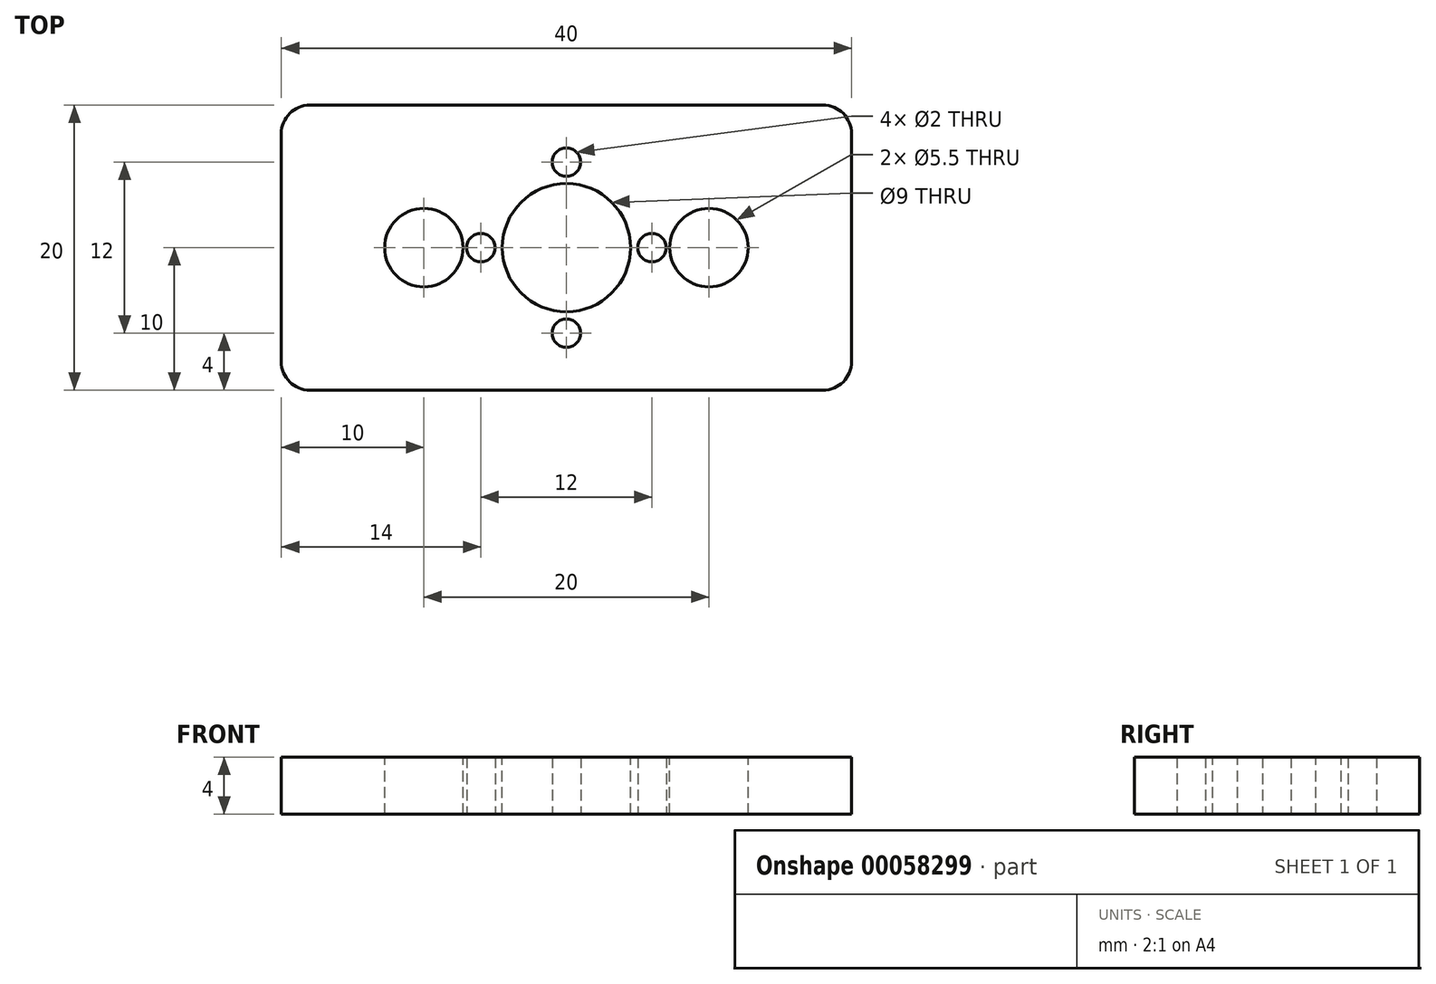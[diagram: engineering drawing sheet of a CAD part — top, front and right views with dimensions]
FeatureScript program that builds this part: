
annotation { "Feature Type Name" : "Feature", "Feature Type Description" : "" }
export const myFeature = defineFeature(function(context is Context, id is Id, definition is map)
    precondition{}
    {
        {
            var Q0;
            Q0=qCreatedBy(makeId("Top.planeOp"),FACE);
            var sketch = newSketch(context, id + "F6", { "sketchPlane" : qUnion([Q0])});
            skLineSegment(sketch, "E0.rect.bottom", {"start": v(20, -10) * mm, "end": v(-20, -10) * mm});
            skLineSegment(sketch, "E0.rect.top", {"start": v(20, 10) * mm, "end": v(-20, 10) * mm});
            skLineSegment(sketch, "E0.rect.left", {"start": v(20, -10) * mm, "end": v(20, 10) * mm});
            skLineSegment(sketch, "E0.rect.right", {"start": v(-20, -10) * mm, "end": v(-20, 10) * mm});
            skPoint(sketch, "E0.rect.middle", {"position": v(0, 0) * mm});
            skCircle(sketch, "E1", {"center": v(0, 0) * mm, "radius": 6 * mm});
            skPoint(sketch, "E2", {"position": v(0, 6) * mm});
            skPoint(sketch, "E3", {"position": v(6, 0) * mm});
            skPoint(sketch, "E4", {"position": v(0, -6) * mm});
            skPoint(sketch, "E5", {"position": v(-6, 0) * mm});
            skSolve(sketch);
        }
        {
            var Q0;
            Q0=makeQuery(id+"F6.imprint","IMPRINT",FACE,{"disambiguationData":[TD([[makeQuery(id+"F6.imprint","IMPRINT",EDGE,{"derivedFrom":sQuery(id+"F6.wireOp",EDGE,"E0.rect.bottom")}),-1.0]])]});
            var Q1;
            Q1=makeQuery(id+"F6.imprint","IMPRINT",FACE,{"disambiguationData":[TD([[makeQuery(id+"F6.imprint","IMPRINT",EDGE,{"derivedFrom":sQuery(id+"F6.wireOp",EDGE,"E1")}),1.0]])]});
            extrude(context, id + "F7", {"entities" : qUnion([Q0, Q1]), "depth" : 4 * mm});
        }
        {
            var Q0;
            Q0=sQuery(id+"F6.wireOp",VERTEX,"E4");
            var Q1;
            Q1=sQuery(id+"F6.wireOp",VERTEX,"E5");
            var Q2;
            Q2=sQuery(id+"F6.wireOp",VERTEX,"E3");
            var Q3;
            Q3=sQuery(id+"F6.wireOp",VERTEX,"E2");
            var Q4;
            Q4=makeQuery(id+"F7.opExtrude","SWEPT_BODY",BODY,{"disambiguationData":[OSD([sQuery(id+"F6.wireOp",EDGE,"E0.rect.bottom"),sQuery(id+"F6.wireOp",EDGE,"E0.rect.top"),sQuery(id+"F6.wireOp",EDGE,"E0.rect.left"),sQuery(id+"F6.wireOp",EDGE,"E0.rect.right")])]});
            hole(context, id + "F0", {"style" : HoleStyle.SIMPLE, "holeDiameter" : 2 * mm, "endStyle" : HoleEndStyle.THROUGH, "oppositeDirection" : true, "locations" : qUnion([Q0, Q1, Q2, Q3]), "scope" : qUnion([Q4])});
        }
        {
            var Q0;
            Q0=makeQuery(id+"F7.opExtrude","CAP_FACE",FACE,{"disambiguationData":[OSD([sQuery(id+"F6.wireOp",EDGE,"E0.rect.bottom"),sQuery(id+"F6.wireOp",EDGE,"E0.rect.top"),sQuery(id+"F6.wireOp",EDGE,"E0.rect.left"),sQuery(id+"F6.wireOp",EDGE,"E0.rect.right")])],"isStart":false});
            var sketch = newSketch(context, id + "F8", { "sketchPlane" : qUnion([Q0])});
            skPoint(sketch, "E6", {"position": v(0, 0) * mm});
            skSolve(sketch);
        }
        {
            var Q0;
            Q0=sQuery(id+"F8.wireOp",VERTEX,"E6");
            var Q1;
            Q1=makeQuery(id+"F7.opExtrude","SWEPT_BODY",BODY,{"disambiguationData":[OSD([sQuery(id+"F6.wireOp",EDGE,"E0.rect.bottom"),sQuery(id+"F6.wireOp",EDGE,"E0.rect.top"),sQuery(id+"F6.wireOp",EDGE,"E0.rect.left"),sQuery(id+"F6.wireOp",EDGE,"E0.rect.right")])]});
            hole(context, id + "F1", {"style" : HoleStyle.SIMPLE, "holeDiameter" : 9 * mm, "endStyle" : HoleEndStyle.THROUGH, "locations" : qUnion([Q0]), "scope" : qUnion([Q1])});
        }
        {
            var Q0;
            Q0=makeQuery(id+"F7.opExtrude","SWEPT_EDGE",EDGE,{"disambiguationData":[OSD([sQuery(id+"F6.wireOp",EDGE,"E0.rect.top"),sQuery(id+"F6.wireOp",EDGE,"E0.rect.left")])]});
            var Q1;
            Q1=makeQuery(id+"F7.opExtrude","SWEPT_EDGE",EDGE,{"disambiguationData":[OSD([sQuery(id+"F6.wireOp",EDGE,"E0.rect.bottom"),sQuery(id+"F6.wireOp",EDGE,"E0.rect.left")])]});
            var Q2;
            Q2=makeQuery(id+"F7.opExtrude","SWEPT_EDGE",EDGE,{"disambiguationData":[OSD([sQuery(id+"F6.wireOp",EDGE,"E0.rect.bottom"),sQuery(id+"F6.wireOp",EDGE,"E0.rect.right")])]});
            var Q3;
            Q3=makeQuery(id+"F7.opExtrude","SWEPT_EDGE",EDGE,{"disambiguationData":[OSD([sQuery(id+"F6.wireOp",EDGE,"E0.rect.top"),sQuery(id+"F6.wireOp",EDGE,"E0.rect.right")])]});
            fillet(context, id + "F2", {"entities" : qUnion([Q0, Q1, Q2, Q3]), "radius" : 2 * mm, "tangentPropagation" : true, "allowEdgeOverflow" : false});
        }
        {
            var Q0;
            Q0=makeQuery(id+"F7.opExtrude","CAP_FACE",FACE,{"disambiguationData":[OSD([sQuery(id+"F6.wireOp",EDGE,"E0.rect.bottom"),sQuery(id+"F6.wireOp",EDGE,"E0.rect.top"),sQuery(id+"F6.wireOp",EDGE,"E0.rect.left"),sQuery(id+"F6.wireOp",EDGE,"E0.rect.right")])],"isStart":false});
            var sketch = newSketch(context, id + "F3", { "sketchPlane" : qUnion([Q0])});
            skPoint(sketch, "E7", {"position": v(-10, 0) * mm});
            skPoint(sketch, "E8", {"position": v(10, 0) * mm});
            skSolve(sketch);
        }
        {
            var Q0;
            Q0=sQuery(id+"F3.wireOp",VERTEX,"E8");
            var Q1;
            Q1=sQuery(id+"F3.wireOp",VERTEX,"E7");
            var Q2;
            Q2=makeQuery(id+"F7.opExtrude","SWEPT_BODY",BODY,{"disambiguationData":[OSD([sQuery(id+"F6.wireOp",EDGE,"E0.rect.bottom"),sQuery(id+"F6.wireOp",EDGE,"E0.rect.top"),sQuery(id+"F6.wireOp",EDGE,"E0.rect.left"),sQuery(id+"F6.wireOp",EDGE,"E0.rect.right")])]});
            hole(context, id + "F4", {"style" : HoleStyle.SIMPLE, "holeDiameter" : 5.5 * mm, "endStyle" : HoleEndStyle.THROUGH, "locations" : qUnion([Q0, Q1]), "scope" : qUnion([Q2])});
        }
    });
